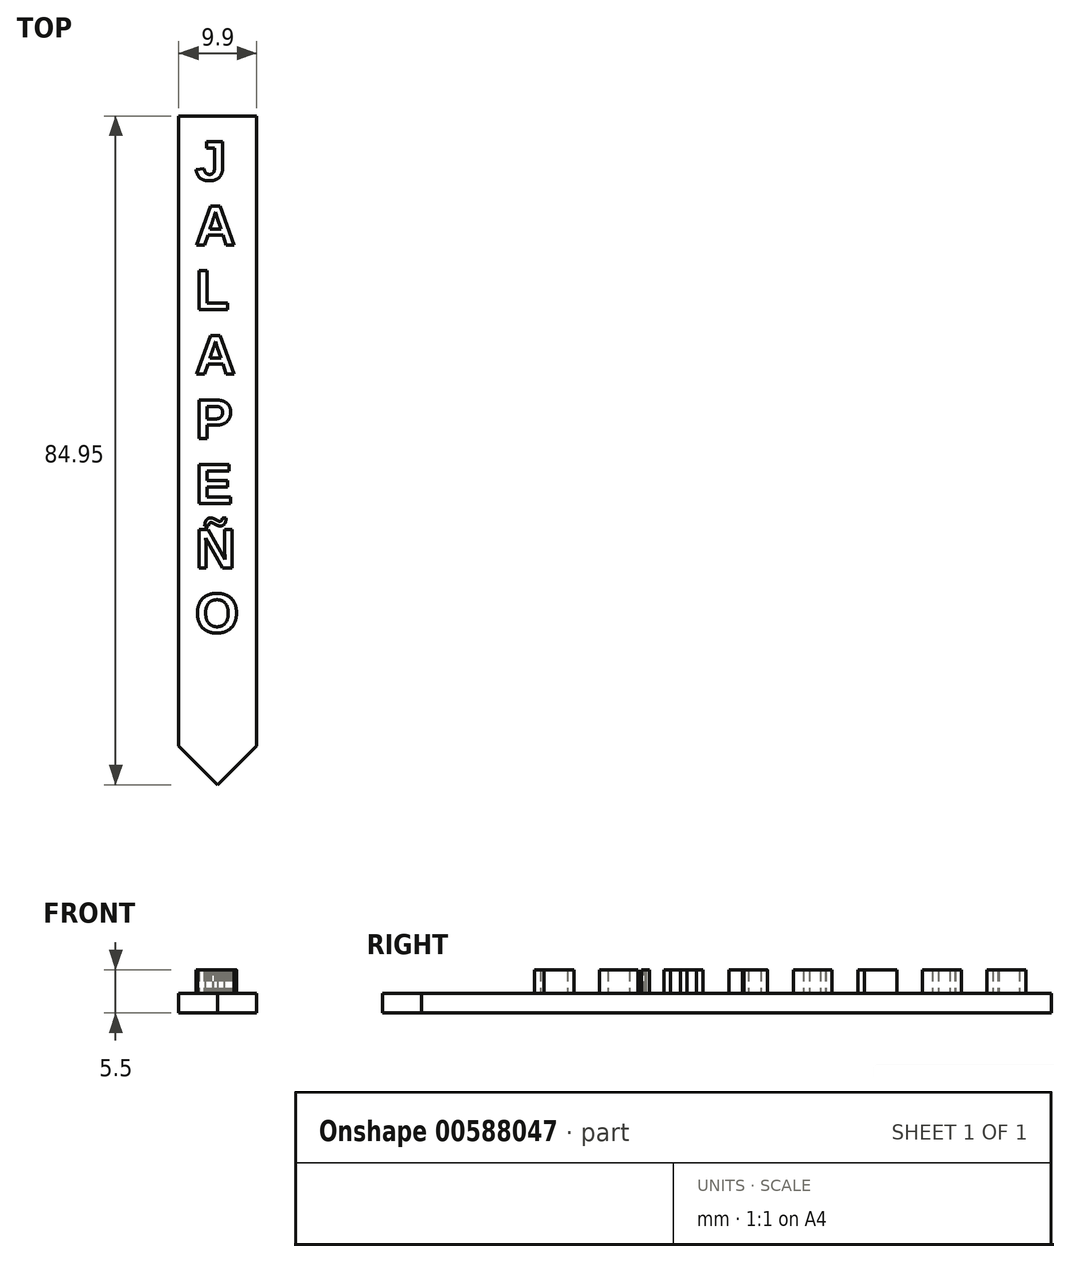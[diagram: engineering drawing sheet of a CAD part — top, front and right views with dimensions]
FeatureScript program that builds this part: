
annotation { "Feature Type Name" : "Feature", "Feature Type Description" : "" }
export const myFeature = defineFeature(function(context is Context, id is Id, definition is map)
    precondition{}
    {
        {
            var Q0;
            Q0=qCreatedBy(makeId("Top.planeOp"),FACE);
            var sketch = newSketch(context, id + "F0", { "sketchPlane" : qUnion([Q0])});
            skLineSegment(sketch, "E0", {"start": v(0, 0) * mm, "end": v(4.95, 4.95) * mm});
            skLineSegment(sketch, "E1", {"start": v(0, 0) * mm, "end": v(-4.95, 4.95) * mm});
            skPoint(sketch, "E2.end.orphan", {"position": v(-3.53, 0) * mm});
            skPoint(sketch, "E3.end.orphan", {"position": v(4.95, 0) * mm});
            skLineSegment(sketch, "E4", {"start": v(4.95, 4.95) * mm, "end": v(4.95, 84.95) * mm});
            skLineSegment(sketch, "E5", {"start": v(-4.95, 4.95) * mm, "end": v(-4.95, 84.95) * mm});
            skLineSegment(sketch, "E6", {"start": v(-4.95, 84.95) * mm, "end": v(4.95, 84.95) * mm});
            skSolve(sketch);
        }
        {
            var Q0;
            Q0 = qSketchRegion(id + "F0", true);
            extrude(context, id + "F1", {"entities" : qUnion([Q0]), "depth" : 2.5 * mm, "offsetDistance" : 25 * mm});
        }
        {
            var Q0;
            Q0=makeQuery(id+"F1.opExtrude","CAP_FACE",FACE,{"disambiguationData":[OSD([sQuery(id+"F0.wireOp",EDGE,"E0"),sQuery(id+"F0.wireOp",EDGE,"E1"),sQuery(id+"F0.wireOp",EDGE,"E4"),sQuery(id+"F0.wireOp",EDGE,"E5"),sQuery(id+"F0.wireOp",EDGE,"E6")])],"isStart":false});
            var sketch = newSketch(context, id + "F2", { "sketchPlane" : qUnion([Q0])});
            skText(sketch, "E7", { "text": "\nA\nL\nA\nP\nE\nÑ\nO", "fontName": "Arimo-Bold.ttf"});
            skText(sketch, "E8", { "text": "J", "fontName": "Arimo-Bold.ttf"});
            const initialGuessF2  = {"E7": [-0.00287, 0.0768, 1, 0, 0.00514], "E8": [-0.00287, 0.0768, 1, 0, 0.00514]};
            skSetInitialGuess(sketch, initialGuessF2);
            skSolve(sketch);
        }
        {
            var Q0;
            Q0 = qSketchRegion(id + "F2", true);
            extrude(context, id + "F3", {"entities" : qUnion([Q0]), "operationType" : NewBodyOperationType.ADD, "depth" : 3 * mm, "offsetDistance" : 25 * mm});
        }
    });
